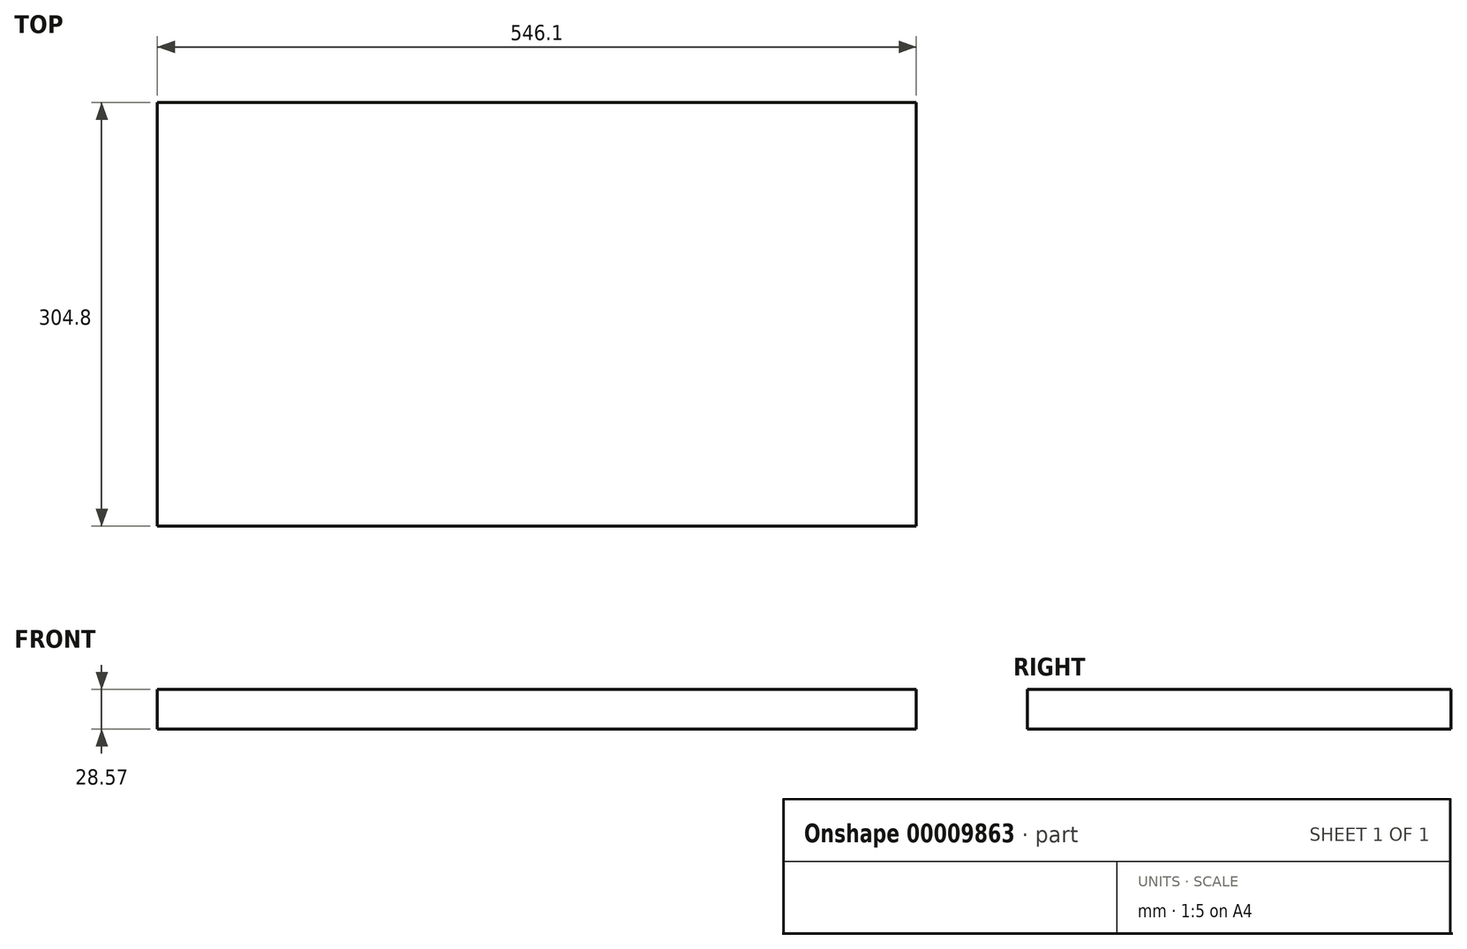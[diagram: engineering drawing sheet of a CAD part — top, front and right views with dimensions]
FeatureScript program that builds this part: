
annotation { "Feature Type Name" : "Feature", "Feature Type Description" : "" }
export const myFeature = defineFeature(function(context is Context, id is Id, definition is map)
    precondition{}
    {
        {
            var Q0;
            Q0=qCreatedBy(makeId("Top.planeOp"),FACE);
            var sketch = newSketch(context, id + "F0", { "sketchPlane" : qUnion([Q0])});
            skLineSegment(sketch, "E0.bottom", {"start": v(-273.05, 152.4) * mm, "end": v(273.05, 152.4) * mm});
            skLineSegment(sketch, "E0.top", {"start": v(-273.05, -152.4) * mm, "end": v(273.05, -152.4) * mm});
            skLineSegment(sketch, "E0.left", {"start": v(-273.05, 152.4) * mm, "end": v(-273.05, -152.4) * mm});
            skLineSegment(sketch, "E0.right", {"start": v(273.05, 152.4) * mm, "end": v(273.05, -152.4) * mm});
            skSolve(sketch);
        }
        {
            var Q0;
            Q0=makeQuery(id+"F0.imprint","IMPRINT",FACE,{"disambiguationData":[TD([[makeQuery(id+"F0.imprint","IMPRINT",EDGE,{"derivedFrom":sQuery(id+"F0.wireOp",EDGE,"E0.bottom")}),-1.0]])]});
            extrude(context, id + "F1", {"entities" : qUnion([Q0]), "depth" : 28.57 * mm});
        }
    });
